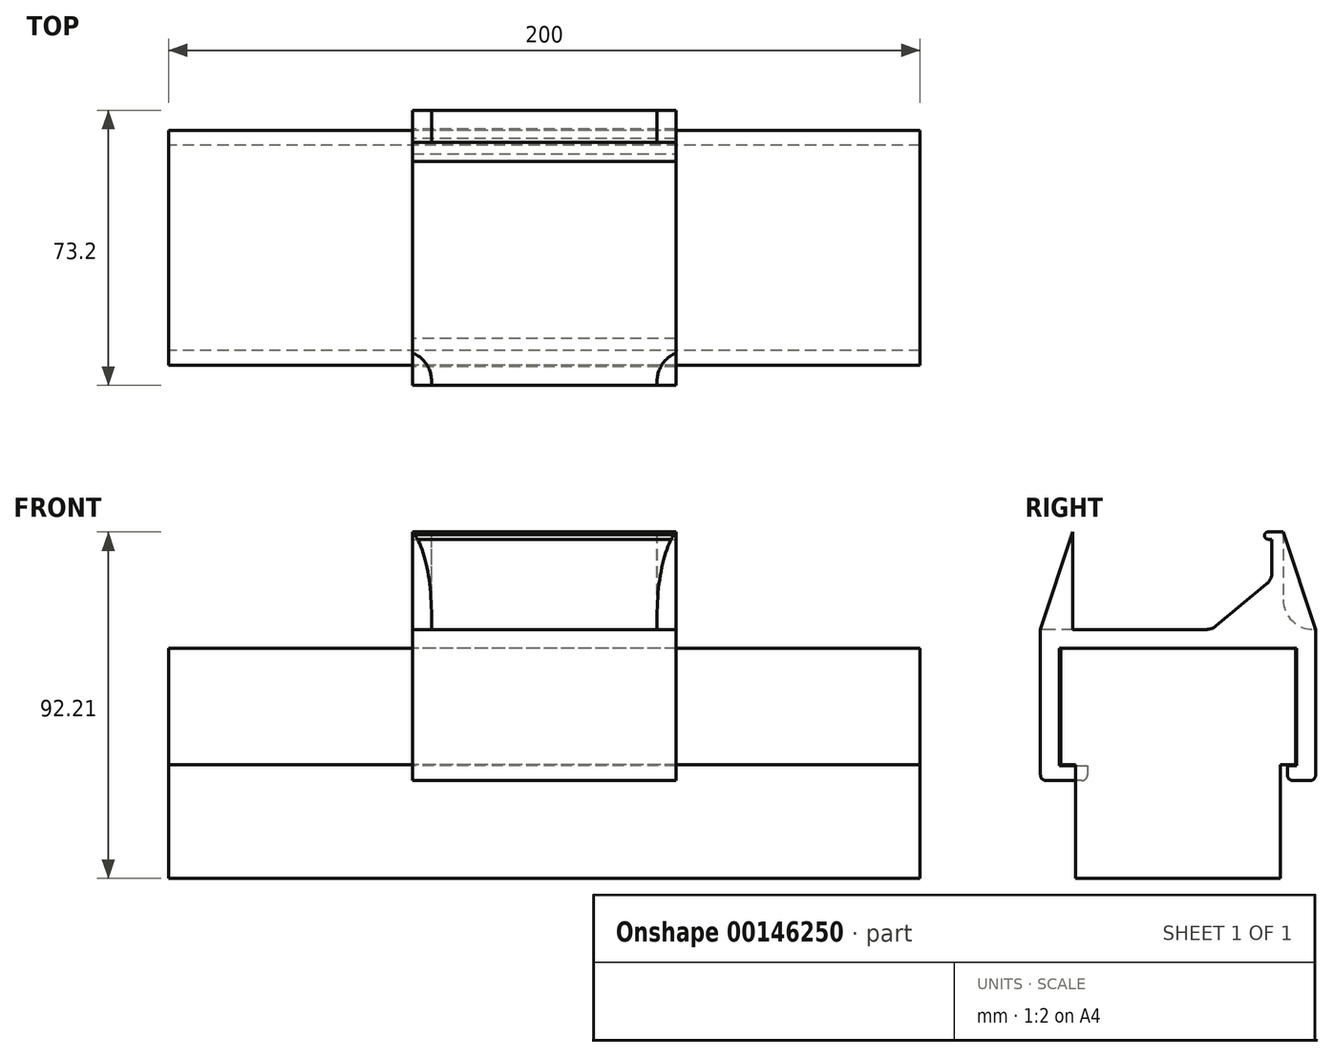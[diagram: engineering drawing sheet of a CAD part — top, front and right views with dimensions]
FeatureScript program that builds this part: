
annotation { "Feature Type Name" : "Feature", "Feature Type Description" : "" }
export const myFeature = defineFeature(function(context is Context, id is Id, definition is map)
    precondition{}
    {
        {
            var Q0;
            Q0=qCreatedBy(makeId("Right.planeOp"),FACE);
            var sketch = newSketch(context, id + "F0", { "sketchPlane" : qUnion([Q0])});
            skLineSegment(sketch, "E0.bottom", {"start": v(-31.25, 0) * mm, "end": v(31.25, 0) * mm});
            skLineSegment(sketch, "E0.top", {"start": v(-31.25, -31) * mm, "end": v(31.25, -31) * mm});
            skLineSegment(sketch, "E0.left", {"start": v(-31.25, 0) * mm, "end": v(-31.25, -31) * mm});
            skLineSegment(sketch, "E0.right", {"start": v(31.25, 0) * mm, "end": v(31.25, -31) * mm});
            skLineSegment(sketch, "E1", {"start": v(27.25, -31) * mm, "end": v(27.25, -61.26) * mm});
            skLineSegment(sketch, "E2", {"start": v(27.25, -61.26) * mm, "end": v(-27.25, -61.26) * mm});
            skLineSegment(sketch, "E3", {"start": v(-27.25, -61.26) * mm, "end": v(-27.25, -31) * mm});
            skSolve(sketch);
        }
        {
            var Q0;
            Q0=makeQuery(id+"F0.imprint","IMPRINT",FACE,{"disambiguationData":[TD([[makeQuery(id+"F0.imprint","IMPRINT",EDGE,{"derivedFrom":sQuery(id+"F0.wireOp",EDGE,"E0.bottom")}),-1.0]])]});
            var Q1;
            {var subQ0=sQuery(id+"F0.wireOp",EDGE,"E1");Q1=makeQuery(id+"F0.imprint","IMPRINT",FACE,{"disambiguationData":[TD([[makeQuery(id+"F0.imprint","IMPRINT",EDGE,{"derivedFrom":subQ0}),-1.0]])]});}
            extrude(context, id + "F1", {"entities" : qUnion([Q0, Q1]), "endBound" : BoundingType.SYMMETRIC, "depth" : 200 * mm});
        }
        {
            var Q0;
            Q0=qCreatedBy(makeId("Right.planeOp"),FACE);
            var sketch = newSketch(context, id + "F2", { "sketchPlane" : qUnion([Q0])});
            skLineSegment(sketch, "E4", {"start": v(0, 0) * mm, "end": v(31.6, 0) * mm});
            skLineSegment(sketch, "E5", {"start": v(31.6, 0) * mm, "end": v(31.6, -31.2) * mm});
            skLineSegment(sketch, "E6", {"start": v(31.6, -31.2) * mm, "end": v(29.1, -31.2) * mm});
            skLineSegment(sketch, "E7", {"start": v(29.1, -31.2) * mm, "end": v(29.1, -35.2) * mm});
            skLineSegment(sketch, "E8", {"start": v(29.1, -35.2) * mm, "end": v(36.6, -35.2) * mm});
            skLineSegment(sketch, "E9", {"start": v(36.6, -35.2) * mm, "end": v(36.6, 5) * mm});
            skLineSegment(sketch, "E10", {"start": v(36.6, 5) * mm, "end": v(0, 5) * mm});
            skLineSegment(sketch, "E11", {"start": v(0, 5) * mm, "end": v(0, 0) * mm});
            skLineSegment(sketch, "E12.MirrorCS", {"start": v(-36.6, 5) * mm, "end": v(0, 5) * mm});
            skLineSegment(sketch, "E13.MirrorCS", {"start": v(0, 0) * mm, "end": v(-31.6, 0) * mm});
            skLineSegment(sketch, "E14.MirrorCS", {"start": v(-31.6, 0) * mm, "end": v(-31.6, -31.2) * mm});
            skLineSegment(sketch, "E15.MirrorCS", {"start": v(-31.6, -31.2) * mm, "end": v(-29.1, -31.2) * mm});
            skLineSegment(sketch, "E16.MirrorCS", {"start": v(-29.1, -31.2) * mm, "end": v(-29.1, -35.2) * mm});
            skLineSegment(sketch, "E17.MirrorCS", {"start": v(-29.1, -35.2) * mm, "end": v(-36.6, -35.2) * mm});
            skLineSegment(sketch, "E18.MirrorCS", {"start": v(-36.6, -35.2) * mm, "end": v(-36.6, 5) * mm});
            skLineSegment(sketch, "E19", {"start": v(-29.1, -31.2) * mm, "end": v(-24.1, -31.2) * mm});
            skLineSegment(sketch, "E20", {"start": v(-24.1, -31.2) * mm, "end": v(-24.1, -35.2) * mm});
            skLineSegment(sketch, "E21", {"start": v(-24.1, -35.2) * mm, "end": v(-29.1, -35.2) * mm});
            skSolve(sketch);
        }
        {
            var Q0;
            Q0 = qSketchRegion(id + "F2", true);
            extrude(context, id + "F3", {"entities" : qUnion([Q0]), "endBound" : BoundingType.SYMMETRIC, "depth" : 70 * mm});
        }
        {
            var Q0;
            Q0=makeQuery(id+"F3.opExtrude","CAP_FACE",FACE,{"disambiguationData":[OSD([sQuery(id+"F2.wireOp",EDGE,"E4"),sQuery(id+"F2.wireOp",EDGE,"E5"),sQuery(id+"F2.wireOp",EDGE,"E6"),sQuery(id+"F2.wireOp",EDGE,"E7"),sQuery(id+"F2.wireOp",EDGE,"E8"),sQuery(id+"F2.wireOp",EDGE,"E9"),sQuery(id+"F2.wireOp",EDGE,"E10"),sQuery(id+"F2.wireOp",EDGE,"E12.MirrorCS"),sQuery(id+"F2.wireOp",EDGE,"E13.MirrorCS"),sQuery(id+"F2.wireOp",EDGE,"E14.MirrorCS"),sQuery(id+"F2.wireOp",EDGE,"E15.MirrorCS"),sQuery(id+"F2.wireOp",EDGE,"E16.MirrorCS"),sQuery(id+"F2.wireOp",EDGE,"E17.MirrorCS"),sQuery(id+"F2.wireOp",EDGE,"E18.MirrorCS")])],"isStart":false});
            var sketch = newSketch(context, id + "F4", { "sketchPlane" : qUnion([Q0])});
            skLineSegment(sketch, "E22.top", {"start": v(-25, 5) * mm, "end": v(25, 5) * mm, "construction": true});
            skLineSegment(sketch, "E22.right", {"start": v(25, 29) * mm, "end": v(25, 5) * mm});
            skLineSegment(sketch, "E23", {"start": v(0, 0) * mm, "end": v(0, 28) * mm});
            skLineSegment(sketch, "E24", {"start": v(0, 5) * mm, "end": v(7.55, 5) * mm});
            skLineSegment(sketch, "E25", {"start": v(10.11, 5.92) * mm, "end": v(23.56, 17.1) * mm});
            skLineSegment(sketch, "E26", {"start": v(25, 20.18) * mm, "end": v(25, 29) * mm});
            skLineSegment(sketch, "E27", {"start": v(23.01, 30.17) * mm, "end": v(23.02, 30.22) * mm});
            skLineSegment(sketch, "E28", {"start": v(23.99, 30.95) * mm, "end": v(28, 30.95) * mm});
            skLineSegment(sketch, "E29", {"start": v(28, 30.95) * mm, "end": v(28, 5) * mm});
            skLineSegment(sketch, "E30", {"start": v(24, 29) * mm, "end": v(25, 29) * mm});
            skPoint(sketch, "E31.visualSharp", {"position": v(9, 5) * mm});
            skArc(sketch, "E31.filletArc", {"start": v(7.55, 5) * mm, "mid": v(8.91, 5.24) * mm, "end": v(10.11, 5.92) * mm});
            skPoint(sketch, "E32.visualSharp", {"position": v(25, 18.3) * mm});
            skArc(sketch, "E32.filletArc", {"start": v(23.56, 17.1) * mm, "mid": v(24.62, 18.48) * mm, "end": v(25, 20.18) * mm});
            skPoint(sketch, "E33.visualSharp", {"position": v(23.19, 30.95) * mm});
            skArc(sketch, "E33.filletArc", {"start": v(23.99, 30.95) * mm, "mid": v(23.36, 30.73) * mm, "end": v(23.01, 30.17) * mm});
            skPoint(sketch, "E34.visualSharp", {"position": v(22.75, 29) * mm});
            skArc(sketch, "E34.filletArc", {"start": v(23.02, 30.22) * mm, "mid": v(23.22, 29.38) * mm, "end": v(24, 29) * mm});
            skArc(sketch, "E35.MirrorCS", {"start": v(-7.55, 5) * mm, "mid": v(-8.91, 5.24) * mm, "end": v(-10.11, 5.92) * mm});
            skLineSegment(sketch, "E36.MirrorCS", {"start": v(-24, 29) * mm, "end": v(-25, 29) * mm});
            skArc(sketch, "E37.MirrorCS", {"start": v(-23.02, 30.22) * mm, "mid": v(-23.22, 29.38) * mm, "end": v(-24, 29) * mm});
            skArc(sketch, "E38.MirrorCS", {"start": v(-23.56, 17.1) * mm, "mid": v(-24.62, 18.48) * mm, "end": v(-25, 20.18) * mm});
            skArc(sketch, "E39.MirrorCS", {"start": v(-23.99, 30.95) * mm, "mid": v(-23.36, 30.73) * mm, "end": v(-23.01, 30.17) * mm});
            skPoint(sketch, "E40.MirrorP", {"position": v(-25, 18.3) * mm});
            skLineSegment(sketch, "E41.MirrorCS", {"start": v(-25, 20.18) * mm, "end": v(-25, 29) * mm});
            skLineSegment(sketch, "E42.MirrorCS", {"start": v(-23.99, 30.95) * mm, "end": v(-28, 30.95) * mm});
            skPoint(sketch, "E43.MirrorP", {"position": v(-22.75, 29) * mm});
            skPoint(sketch, "E44.MirrorP", {"position": v(-23.19, 30.95) * mm});
            skLineSegment(sketch, "E45.MirrorCS", {"start": v(-28, 30.95) * mm, "end": v(-28, 5) * mm});
            skLineSegment(sketch, "E46.MirrorCS", {"start": v(-10.11, 5.92) * mm, "end": v(-23.56, 17.1) * mm});
            skSolve(sketch);
        }
        {
            var Q0;
            {var subQ0=sQuery(id+"F4.wireOp",EDGE,"E35.MirrorCS");Q0=makeQuery(id+"F4.imprint","IMPRINT",FACE,{"disambiguationData":[TD([[makeQuery(id+"F4.imprint","IMPRINT",EDGE,{"derivedFrom":subQ0}),1.0]])]});}
            var Q1;
            {var subQ1=sQuery(id+"F4.wireOp",EDGE,"E22.right");Q1=makeQuery(id+"F4.imprint","IMPRINT",FACE,{"disambiguationData":[TD([[makeQuery(id+"F4.imprint","IMPRINT",EDGE,{"derivedFrom":subQ1}),-1.0]])]});}
            var Q2;
            {var subQ1=sQuery(id+"F4.wireOp",EDGE,"E22.right");Q2=makeQuery(id+"F4.imprint","IMPRINT",FACE,{"disambiguationData":[TD([[makeQuery(id+"F4.imprint","IMPRINT",EDGE,{"derivedFrom":subQ1}),1.0]])]});}
            var Q3;
            Q3=makeQuery(id+"F3.opExtrude","CAP_FACE",FACE,{"disambiguationData":[OSD([sQuery(id+"F2.wireOp",EDGE,"E4"),sQuery(id+"F2.wireOp",EDGE,"E5"),sQuery(id+"F2.wireOp",EDGE,"E6"),sQuery(id+"F2.wireOp",EDGE,"E7"),sQuery(id+"F2.wireOp",EDGE,"E8"),sQuery(id+"F2.wireOp",EDGE,"E9"),sQuery(id+"F2.wireOp",EDGE,"E10"),sQuery(id+"F2.wireOp",EDGE,"E12.MirrorCS"),sQuery(id+"F2.wireOp",EDGE,"E13.MirrorCS"),sQuery(id+"F2.wireOp",EDGE,"E14.MirrorCS"),sQuery(id+"F2.wireOp",EDGE,"E15.MirrorCS"),sQuery(id+"F2.wireOp",EDGE,"E16.MirrorCS"),sQuery(id+"F2.wireOp",EDGE,"E17.MirrorCS"),sQuery(id+"F2.wireOp",EDGE,"E18.MirrorCS")])],"isStart":true});
            extrude(context, id + "F5", {"entities" : qUnion([Q0, Q1, Q2]), "endBound" : BoundingType.UP_TO_SURFACE, "oppositeDirection" : true, "endBoundEntityFace" : qUnion([Q3]), "depth" : 45 * mm});
        }
        {
            var Q0;
            Q0=makeQuery(id+"F5.opExtrude","SWEPT_BODY",BODY,{"disambiguationData":[OSD([sQuery(id+"F2.wireOp",EDGE,"E10"),sQuery(id+"F2.wireOp",EDGE,"E12.MirrorCS"),sQuery(id+"F4.wireOp",EDGE,"E25"),sQuery(id+"F4.wireOp",EDGE,"E26"),sQuery(id+"F4.wireOp",EDGE,"E27"),sQuery(id+"F4.wireOp",EDGE,"E28"),sQuery(id+"F4.wireOp",EDGE,"E29"),sQuery(id+"F4.wireOp",EDGE,"E30"),sQuery(id+"F4.wireOp",EDGE,"E31.filletArc"),sQuery(id+"F4.wireOp",EDGE,"E32.filletArc")])]});
            var Q1;
            Q1=makeQuery(id+"F5.opExtrude","SWEPT_BODY",BODY,{"disambiguationData":[OSD([sQuery(id+"F2.wireOp",EDGE,"E10"),sQuery(id+"F2.wireOp",EDGE,"E12.MirrorCS"),sQuery(id+"F4.wireOp",EDGE,"03d504c9-1d4a-4a00-808c-d90ce03fa8d20.MirrorCS"),sQuery(id+"F4.wireOp",EDGE,"03d504c9-1d4a-4a00-808c-d90ce03fa8d21.MirrorCS"),sQuery(id+"F4.wireOp",EDGE,"03d504c9-1d4a-4a00-808c-d90ce03fa8d22.MirrorCS"),sQuery(id+"F4.wireOp",EDGE,"03d504c9-1d4a-4a00-808c-d90ce03fa8d23.MirrorCS"),sQuery(id+"F4.wireOp",EDGE,"03d504c9-1d4a-4a00-808c-d90ce03fa8d24.MirrorCS"),sQuery(id+"F4.wireOp",EDGE,"03d504c9-1d4a-4a00-808c-d90ce03fa8d25.MirrorCS"),sQuery(id+"F4.wireOp",EDGE,"03d504c9-1d4a-4a00-808c-d90ce03fa8d26.MirrorCS"),sQuery(id+"F4.wireOp",EDGE,"03d504c9-1d4a-4a00-808c-d90ce03fa8d27.MirrorCS")])]});
            var Q2;
            Q2=makeQuery(id+"F3.opExtrude","SWEPT_BODY",BODY,{"disambiguationData":[OSD([sQuery(id+"F2.wireOp",EDGE,"E4"),sQuery(id+"F2.wireOp",EDGE,"E5"),sQuery(id+"F2.wireOp",EDGE,"E6"),sQuery(id+"F2.wireOp",EDGE,"E7"),sQuery(id+"F2.wireOp",EDGE,"E8"),sQuery(id+"F2.wireOp",EDGE,"E9"),sQuery(id+"F2.wireOp",EDGE,"E10"),sQuery(id+"F2.wireOp",EDGE,"E12.MirrorCS"),sQuery(id+"F2.wireOp",EDGE,"E13.MirrorCS"),sQuery(id+"F2.wireOp",EDGE,"E14.MirrorCS"),sQuery(id+"F2.wireOp",EDGE,"E15.MirrorCS"),sQuery(id+"F2.wireOp",EDGE,"E16.MirrorCS"),sQuery(id+"F2.wireOp",EDGE,"E17.MirrorCS"),sQuery(id+"F2.wireOp",EDGE,"E18.MirrorCS")])]});
            var Q3;
            Q3=makeQuery(id+"F06HoFXVDaUI86O_4.opPattern","COPY",BODY,{"derivedFrom":makeQuery(id+"F5.opExtrude","SWEPT_BODY",BODY,{"disambiguationData":[OSD([sQuery(id+"F2.wireOp",EDGE,"E10"),sQuery(id+"F2.wireOp",EDGE,"E12.MirrorCS"),sQuery(id+"F4.wireOp",EDGE,"E25"),sQuery(id+"F4.wireOp",EDGE,"E26"),sQuery(id+"F4.wireOp",EDGE,"E27"),sQuery(id+"F4.wireOp",EDGE,"E28"),sQuery(id+"F4.wireOp",EDGE,"E29"),sQuery(id+"F4.wireOp",EDGE,"E30"),sQuery(id+"F4.wireOp",EDGE,"E31.filletArc"),sQuery(id+"F4.wireOp",EDGE,"E32.filletArc")])]}),"instanceName":"1"});
            var Q4;
            Q4=makeQuery(id+"F06HoFXVDaUI86O_4.opPattern","COPY",BODY,{"derivedFrom":makeQuery(id+"F5.opExtrude","SWEPT_BODY",BODY,{"disambiguationData":[OSD([sQuery(id+"F2.wireOp",EDGE,"E10"),sQuery(id+"F2.wireOp",EDGE,"E12.MirrorCS"),sQuery(id+"F4.wireOp",EDGE,"03d504c9-1d4a-4a00-808c-d90ce03fa8d20.MirrorCS"),sQuery(id+"F4.wireOp",EDGE,"03d504c9-1d4a-4a00-808c-d90ce03fa8d21.MirrorCS"),sQuery(id+"F4.wireOp",EDGE,"03d504c9-1d4a-4a00-808c-d90ce03fa8d22.MirrorCS"),sQuery(id+"F4.wireOp",EDGE,"03d504c9-1d4a-4a00-808c-d90ce03fa8d23.MirrorCS"),sQuery(id+"F4.wireOp",EDGE,"03d504c9-1d4a-4a00-808c-d90ce03fa8d24.MirrorCS"),sQuery(id+"F4.wireOp",EDGE,"03d504c9-1d4a-4a00-808c-d90ce03fa8d25.MirrorCS"),sQuery(id+"F4.wireOp",EDGE,"03d504c9-1d4a-4a00-808c-d90ce03fa8d26.MirrorCS"),sQuery(id+"F4.wireOp",EDGE,"03d504c9-1d4a-4a00-808c-d90ce03fa8d27.MirrorCS")])]}),"instanceName":"1"});
            booleanBodies(context, id + "F6", {"operationType" : BooleanOperationType.UNION, "tools" : qUnion([Q0, Q1, Q2, Q3, Q4])});
        }
        {
            var Q0;
            {var subQ0=sQuery(id+"F2.wireOp",EDGE,"E12.MirrorCS");var subQ1=sQuery(id+"F2.wireOp",EDGE,"E10");Q0=makeQuery(id+"F6.opBoolean","MERGE",FACE,{"derivedFrom":[makeQuery(id+"F3.opExtrude","CAP_FACE",FACE,{"disambiguationData":[OSD([sQuery(id+"F2.wireOp",EDGE,"E4"),sQuery(id+"F2.wireOp",EDGE,"E5"),sQuery(id+"F2.wireOp",EDGE,"E6"),sQuery(id+"F2.wireOp",EDGE,"E7"),sQuery(id+"F2.wireOp",EDGE,"E8"),sQuery(id+"F2.wireOp",EDGE,"E9"),subQ1,subQ0,sQuery(id+"F2.wireOp",EDGE,"E13.MirrorCS"),sQuery(id+"F2.wireOp",EDGE,"E14.MirrorCS"),sQuery(id+"F2.wireOp",EDGE,"E15.MirrorCS"),sQuery(id+"F2.wireOp",EDGE,"E17.MirrorCS"),sQuery(id+"F2.wireOp",EDGE,"E18.MirrorCS"),sQuery(id+"F2.wireOp",EDGE,"E19"),sQuery(id+"F2.wireOp",EDGE,"E20"),sQuery(id+"F2.wireOp",EDGE,"E21")])],"isStart":false}),makeQuery(id+"F5.opExtrude","CAP_FACE",FACE,{"disambiguationData":[OSD([subQ1,subQ0,sQuery(id+"F4.wireOp",EDGE,"E25"),sQuery(id+"F4.wireOp",EDGE,"E26"),sQuery(id+"F4.wireOp",EDGE,"E28"),sQuery(id+"F4.wireOp",EDGE,"E29"),sQuery(id+"F4.wireOp",EDGE,"E30"),sQuery(id+"F4.wireOp",EDGE,"E31.filletArc"),sQuery(id+"F4.wireOp",EDGE,"E32.filletArc"),sQuery(id+"F4.wireOp",EDGE,"E33.filletArc"),sQuery(id+"F4.wireOp",EDGE,"E34.filletArc")])],"isStart":true}),makeQuery(id+"F5.opExtrude","CAP_FACE",FACE,{"disambiguationData":[OSD([subQ1,subQ0,sQuery(id+"F4.wireOp",EDGE,"E35.MirrorCS"),sQuery(id+"F4.wireOp",EDGE,"E36.MirrorCS"),sQuery(id+"F4.wireOp",EDGE,"E37.MirrorCS"),sQuery(id+"F4.wireOp",EDGE,"E38.MirrorCS"),sQuery(id+"F4.wireOp",EDGE,"E39.MirrorCS"),sQuery(id+"F4.wireOp",EDGE,"E41.MirrorCS"),sQuery(id+"F4.wireOp",EDGE,"E42.MirrorCS"),sQuery(id+"F4.wireOp",EDGE,"E45.MirrorCS"),sQuery(id+"F4.wireOp",EDGE,"E46.MirrorCS")])],"isStart":true})]});}
            var sketch = newSketch(context, id + "F7", { "sketchPlane" : qUnion([Q0])});
            skLineSegment(sketch, "E47", {"start": v(28, 5) * mm, "end": v(36.6, 5) * mm});
            skLineSegment(sketch, "E48", {"start": v(36.6, 5) * mm, "end": v(28, 30.95) * mm});
            skLineSegment(sketch, "E49", {"start": v(28, 30.95) * mm, "end": v(28, 5) * mm});
            skLineSegment(sketch, "E50", {"start": v(-36.6, 5) * mm, "end": v(-28, 5) * mm});
            skLineSegment(sketch, "E51", {"start": v(-28, 5) * mm, "end": v(-28, 30.95) * mm});
            skLineSegment(sketch, "E52", {"start": v(-28, 30.95) * mm, "end": v(-36.6, 5) * mm});
            skSolve(sketch);
        }
        {
            var Q0;
            Q0 = qSketchRegion(id + "F7", true);
            extrude(context, id + "F8", {"entities" : qUnion([Q0]), "operationType" : NewBodyOperationType.ADD, "oppositeDirection" : true, "depth" : 5 * mm});
        }
        {
            var Q0;
            {var subQ0=sQuery(id+"F2.wireOp",EDGE,"E12.MirrorCS");var subQ1=sQuery(id+"F2.wireOp",EDGE,"E10");var subQ2=sQuery(id+"F2.wireOp",EDGE,"E21");var subQ3=sQuery(id+"F2.wireOp",EDGE,"E20");var subQ4=sQuery(id+"F2.wireOp",EDGE,"E19");var subQ5=sQuery(id+"F2.wireOp",EDGE,"E18.MirrorCS");var subQ6=sQuery(id+"F2.wireOp",EDGE,"E17.MirrorCS");var subQ7=sQuery(id+"F2.wireOp",EDGE,"E15.MirrorCS");var subQ8=sQuery(id+"F2.wireOp",EDGE,"E14.MirrorCS");var subQ9=sQuery(id+"F2.wireOp",EDGE,"E13.MirrorCS");var subQ10=sQuery(id+"F2.wireOp",EDGE,"E9");var subQ11=sQuery(id+"F2.wireOp",EDGE,"E8");var subQ12=sQuery(id+"F2.wireOp",EDGE,"E7");var subQ13=sQuery(id+"F2.wireOp",EDGE,"E6");var subQ14=sQuery(id+"F2.wireOp",EDGE,"E5");var subQ15=sQuery(id+"F2.wireOp",EDGE,"E4");Q0=makeQuery(id+"F6.opBoolean","MERGE",FACE,{"derivedFrom":[makeQuery(id+"F3.opExtrude","CAP_FACE",FACE,{"disambiguationData":[OSD([subQ15,subQ14,subQ13,subQ12,subQ11,subQ10,subQ1,subQ0,subQ9,subQ8,subQ7,subQ6,subQ5,subQ4,subQ3,subQ2])],"isStart":true}),makeQuery(id+"F5.opExtrude","CAP_FACE",FACE,{"disambiguationData":[OSD([subQ15,subQ14,subQ13,subQ12,subQ11,subQ10,subQ1,subQ0,subQ9,subQ8,subQ7,subQ6,subQ5,subQ4,subQ3,subQ2]),ownerDisambiguation([makeQuery(id+"F5.opExtrude","SWEPT_BODY",BODY,{"disambiguationData":[OSD([subQ1,subQ0,sQuery(id+"F4.wireOp",EDGE,"E25"),sQuery(id+"F4.wireOp",EDGE,"E26"),sQuery(id+"F4.wireOp",EDGE,"E28"),sQuery(id+"F4.wireOp",EDGE,"E29"),sQuery(id+"F4.wireOp",EDGE,"E30"),sQuery(id+"F4.wireOp",EDGE,"E31.filletArc"),sQuery(id+"F4.wireOp",EDGE,"E32.filletArc"),sQuery(id+"F4.wireOp",EDGE,"E33.filletArc"),sQuery(id+"F4.wireOp",EDGE,"E34.filletArc")])]})])],"isStart":false}),makeQuery(id+"F5.opExtrude","CAP_FACE",FACE,{"disambiguationData":[OSD([subQ15,subQ14,subQ13,subQ12,subQ11,subQ10,subQ1,subQ0,subQ9,subQ8,subQ7,subQ6,subQ5,subQ4,subQ3,subQ2]),ownerDisambiguation([makeQuery(id+"F5.opExtrude","SWEPT_BODY",BODY,{"disambiguationData":[OSD([subQ1,subQ0,sQuery(id+"F4.wireOp",EDGE,"E35.MirrorCS"),sQuery(id+"F4.wireOp",EDGE,"E36.MirrorCS"),sQuery(id+"F4.wireOp",EDGE,"E37.MirrorCS"),sQuery(id+"F4.wireOp",EDGE,"E38.MirrorCS"),sQuery(id+"F4.wireOp",EDGE,"E39.MirrorCS"),sQuery(id+"F4.wireOp",EDGE,"E41.MirrorCS"),sQuery(id+"F4.wireOp",EDGE,"E42.MirrorCS"),sQuery(id+"F4.wireOp",EDGE,"E45.MirrorCS"),sQuery(id+"F4.wireOp",EDGE,"E46.MirrorCS")])]})])],"isStart":false})]});}
            var sketch = newSketch(context, id + "F9", { "sketchPlane" : qUnion([Q0])});
            skLineSegment(sketch, "E53", {"start": v(-36.6, 5) * mm, "end": v(-28, 30.95) * mm});
            skLineSegment(sketch, "E54", {"start": v(-28, 30.95) * mm, "end": v(-28, 5) * mm});
            skLineSegment(sketch, "E55", {"start": v(-28, 5) * mm, "end": v(-36.6, 5) * mm});
            skLineSegment(sketch, "E56", {"start": v(28, 30.95) * mm, "end": v(28, 5) * mm});
            skLineSegment(sketch, "E57", {"start": v(28, 5) * mm, "end": v(36.6, 5) * mm});
            skLineSegment(sketch, "E58", {"start": v(36.6, 5) * mm, "end": v(28, 30.95) * mm});
            skSolve(sketch);
        }
        {
            var Q0;
            Q0 = qSketchRegion(id + "F9", true);
            extrude(context, id + "F10", {"entities" : qUnion([Q0]), "operationType" : NewBodyOperationType.ADD, "oppositeDirection" : true, "depth" : 5 * mm});
        }
        {
            var Q0;
            Q0=makeQuery(id+"F5.opExtrude","SWEPT_EDGE",EDGE,{"disambiguationData":[OSD([sQuery(id+"F2.wireOp",EDGE,"E10"),sQuery(id+"F2.wireOp",EDGE,"E12.MirrorCS"),sQuery(id+"F4.wireOp",EDGE,"E29")])]});
            var Q1;
            Q1=makeQuery(id+"F5.opExtrude","SWEPT_EDGE",EDGE,{"disambiguationData":[OSD([sQuery(id+"F2.wireOp",EDGE,"E10"),sQuery(id+"F2.wireOp",EDGE,"E12.MirrorCS"),sQuery(id+"F4.wireOp",EDGE,"E35.MirrorCS")])]});
            var Q2;
            Q2=makeQuery(id+"F5.opExtrude","SWEPT_EDGE",EDGE,{"disambiguationData":[OSD([sQuery(id+"F2.wireOp",EDGE,"E10"),sQuery(id+"F2.wireOp",EDGE,"E12.MirrorCS"),sQuery(id+"F4.wireOp",EDGE,"E45.MirrorCS")])]});
            var Q3;
            Q3=makeQuery(id+"F8.opExtrude","CAP_EDGE",EDGE,{"disambiguationData":[OSD([sQuery(id+"F7.wireOp",EDGE,"E51")])],"isStart":false});
            var Q4;
            Q4=makeQuery(id+"F10.opExtrude","CAP_EDGE",EDGE,{"disambiguationData":[OSD([sQuery(id+"F9.wireOp",EDGE,"E56")])],"isStart":false});
            var Q5;
            Q5=makeQuery(id+"F8.opExtrude","CAP_EDGE",EDGE,{"disambiguationData":[OSD([sQuery(id+"F7.wireOp",EDGE,"E49")])],"isStart":false});
            var Q6;
            Q6=makeQuery(id+"F10.opExtrude","CAP_EDGE",EDGE,{"disambiguationData":[OSD([sQuery(id+"F9.wireOp",EDGE,"E54")])],"isStart":false});
            fillet(context, id + "F11", {"entities" : qUnion([Q0, Q1, Q2, Q3, Q4, Q5, Q6]), "radius" : 8 * mm, "tangentPropagation" : true, "allowEdgeOverflow" : false});
        }
        {
            var Q0;
            Q0=makeQuery(id+"F3.opExtrude","SWEPT_EDGE",EDGE,{"disambiguationData":[OSD([sQuery(id+"F2.wireOp",EDGE,"E17.MirrorCS"),sQuery(id+"F2.wireOp",EDGE,"E18.MirrorCS")])]});
            var Q1;
            Q1=makeQuery(id+"F3.opExtrude","SWEPT_EDGE",EDGE,{"disambiguationData":[OSD([sQuery(id+"F2.wireOp",EDGE,"E8"),sQuery(id+"F2.wireOp",EDGE,"E9")])]});
            var Q2;
            Q2=makeQuery(id+"F3.opExtrude","SWEPT_EDGE",EDGE,{"disambiguationData":[OSD([sQuery(id+"F2.wireOp",EDGE,"E7"),sQuery(id+"F2.wireOp",EDGE,"E8")])]});
            var Q3;
            Q3=makeQuery(id+"F3.opExtrude","SWEPT_EDGE",EDGE,{"disambiguationData":[OSD([sQuery(id+"F2.wireOp",EDGE,"E17.MirrorCS"),sQuery(id+"F2.wireOp",EDGE,"E18.MirrorCS")])]});
            var Q4;
            Q4=makeQuery(id+"F3.opExtrude","SWEPT_EDGE",EDGE,{"disambiguationData":[OSD([sQuery(id+"F2.wireOp",EDGE,"E20"),sQuery(id+"F2.wireOp",EDGE,"E21")])]});
            fillet(context, id + "F12", {"entities" : qUnion([Q0, Q1, Q2, Q3, Q4]), "radius" : 1.5 * mm, "tangentPropagation" : true, "allowEdgeOverflow" : false});
        }
    });
